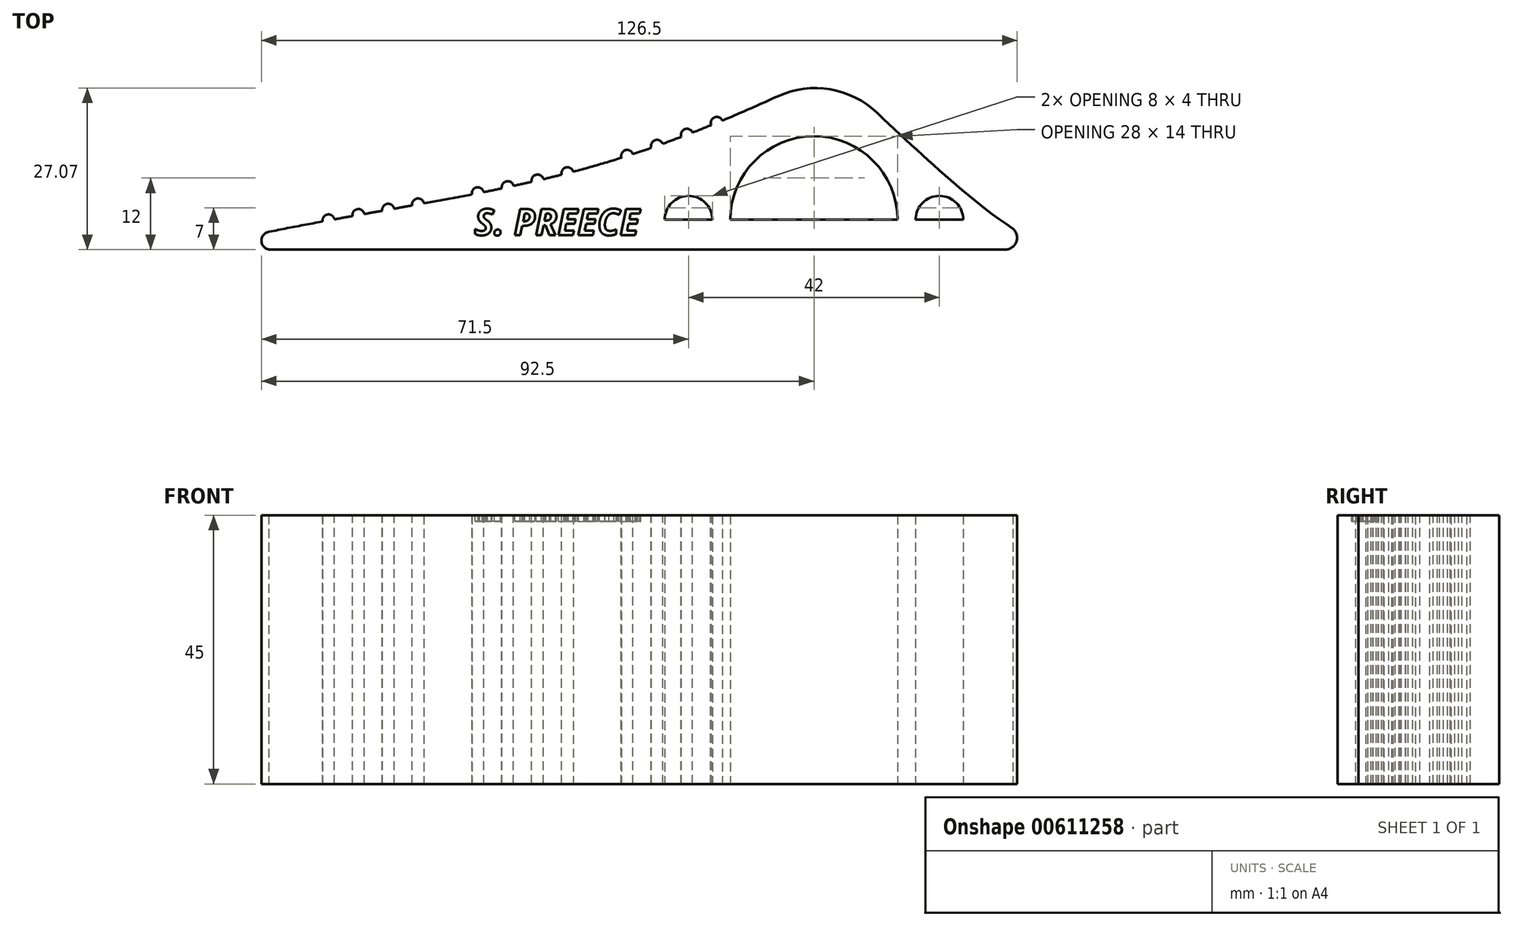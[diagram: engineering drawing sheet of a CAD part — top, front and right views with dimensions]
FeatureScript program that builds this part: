
annotation { "Feature Type Name" : "Feature", "Feature Type Description" : "" }
export const myFeature = defineFeature(function(context is Context, id is Id, definition is map)
    precondition{}
    {
        {
            var Q0;
            Q0=qCreatedBy(makeId("Top.planeOp"),FACE);
            var sketch = newSketch(context, id + "F0", { "sketchPlane" : qUnion([Q0])});
            skLineSegment(sketch, "E0", {"start": v(-38, 0) * mm, "end": v(85, 0) * mm});
            skPoint(sketch, "E1.visualSharp", {"position": v(-56.52, 0) * mm});
            skArc(sketch, "E1.filletArc", {"start": v(-38.27, 2.97) * mm, "mid": v(-39.5, 1.36) * mm, "end": v(-38, 0) * mm});
            skPoint(sketch, "E2.visualSharp", {"position": v(89.83, 0) * mm});
            skArc(sketch, "E2.filletArc", {"start": v(85, 0) * mm, "mid": v(86.88, 1.3) * mm, "end": v(86.3, 3.52) * mm});
            skLineSegment(sketch, "E3", {"start": v(39, 5) * mm, "end": v(67, 5) * mm});
            skArc(sketch, "E4", {"start": v(67, 5) * mm, "mid": v(53, 19) * mm, "end": v(39, 5) * mm});
            skLineSegment(sketch, "E5", {"start": v(28, 5) * mm, "end": v(36, 5) * mm});
            skArc(sketch, "E6", {"start": v(36, 5) * mm, "mid": v(32, 9) * mm, "end": v(28, 5) * mm});
            skArc(sketch, "E7.MirrorCS", {"start": v(70, 5) * mm, "mid": v(74, 9) * mm, "end": v(78, 5) * mm});
            skLineSegment(sketch, "E8.MirrorCS", {"start": v(78, 5) * mm, "end": v(70, 5) * mm});
            skFitSpline(sketch, "E9", {"points": [v(-38.27, 2.97) * mm, v(15.47, 13.8) * mm, v(56.42, 30.22) * mm], "startDerivative": vector(104, 21.18) * mm, "endDerivative": vector(77.97, 38.18) * mm});
            skPoint(sketch, "E10.1.internal.snap0", {"position": v(71.36, 16.87) * mm});
            skFitSpline(sketch, "E10", {"points": [v(56.42, 30.22) * mm, v(71.36, 15.67) * mm, v(86.3, 3.52) * mm], "startDerivative": vector(31.6, -34.36) * mm, "endDerivative": vector(35.04, -23.4) * mm});
            skArc(sketch, "E11.filletArc", {"start": v(63.6, 22.86) * mm, "mid": v(55.7, 26.85) * mm, "end": v(46.93, 25.7) * mm});
            skSolve(sketch);
        }
        {
            var Q0;
            Q0=makeQuery(id+"F0.imprint","IMPRINT",FACE,{"disambiguationData":[TD([[makeQuery(id+"F0.imprint","IMPRINT",EDGE,{"derivedFrom":sQuery(id+"F0.wireOp",EDGE,"E0")}),1.0]])]});
            extrude(context, id + "F1", {"entities" : qUnion([Q0]), "depth" : 45 * mm, "offsetDistance" : 25 * mm});
        }
        {
            var Q0;
            Q0=makeQuery(id+"F1.opExtrude","CAP_FACE",FACE,{"disambiguationData":[OSD([sQuery(id+"F0.wireOp",EDGE,"E0"),sQuery(id+"F0.wireOp",EDGE,"E1.filletArc"),sQuery(id+"F0.wireOp",EDGE,"E2.filletArc"),sQuery(id+"F0.wireOp",EDGE,"E3"),sQuery(id+"F0.wireOp",EDGE,"E4"),sQuery(id+"F0.wireOp",EDGE,"E5"),sQuery(id+"F0.wireOp",EDGE,"E6"),sQuery(id+"F0.wireOp",EDGE,"E7.MirrorCS"),sQuery(id+"F0.wireOp",EDGE,"E8.MirrorCS"),sQuery(id+"F0.wireOp",EDGE,"E9"),sQuery(id+"F0.wireOp",EDGE,"E10"),sQuery(id+"F0.wireOp",EDGE,"E11.filletArc")])],"isStart":false});
            var sketch = newSketch(context, id + "F2", { "sketchPlane" : qUnion([Q0])});
            skCircle(sketch, "E12", {"center": v(-28.27, 4.9) * mm, "radius": 1 * mm});
            skCircle(sketch, "E13", {"center": v(-23.27, 5.8) * mm, "radius": 1 * mm});
            skCircle(sketch, "E14", {"center": v(-18.27, 6.68) * mm, "radius": 1 * mm});
            skCircle(sketch, "E15", {"center": v(-13.27, 7.57) * mm, "radius": 1 * mm});
            skCircle(sketch, "E16", {"center": v(-3.27, 9.44) * mm, "radius": 1 * mm});
            skCircle(sketch, "E17", {"center": v(1.73, 10.46) * mm, "radius": 1 * mm});
            skCircle(sketch, "E18", {"center": v(6.73, 11.57) * mm, "radius": 1 * mm});
            skCircle(sketch, "E19", {"center": v(11.73, 12.8) * mm, "radius": 1 * mm});
            skCircle(sketch, "E20", {"center": v(21.73, 15.7) * mm, "radius": 1 * mm});
            skCircle(sketch, "E21", {"center": v(26.73, 17.4) * mm, "radius": 1 * mm});
            skCircle(sketch, "E22", {"center": v(31.73, 19.25) * mm, "radius": 1 * mm});
            skCircle(sketch, "E23", {"center": v(36.73, 21.24) * mm, "radius": 1 * mm});
            skSolve(sketch);
        }
        {
            var Q0;
            Q0 = qSketchRegion(id + "F2", true);
            var Q1;
            Q1=makeQuery(id+"F1.opExtrude","CAP_FACE",FACE,{"disambiguationData":[OSD([sQuery(id+"F0.wireOp",EDGE,"E0"),sQuery(id+"F0.wireOp",EDGE,"E1.filletArc"),sQuery(id+"F0.wireOp",EDGE,"E2.filletArc"),sQuery(id+"F0.wireOp",EDGE,"E3"),sQuery(id+"F0.wireOp",EDGE,"E4"),sQuery(id+"F0.wireOp",EDGE,"E5"),sQuery(id+"F0.wireOp",EDGE,"E6"),sQuery(id+"F0.wireOp",EDGE,"E7.MirrorCS"),sQuery(id+"F0.wireOp",EDGE,"E8.MirrorCS"),sQuery(id+"F0.wireOp",EDGE,"E9"),sQuery(id+"F0.wireOp",EDGE,"E10"),sQuery(id+"F0.wireOp",EDGE,"E11.filletArc")])],"isStart":true});
            extrude(context, id + "F3", {"entities" : qUnion([Q0]), "operationType" : NewBodyOperationType.ADD, "endBound" : BoundingType.UP_TO_SURFACE, "oppositeDirection" : true, "depth" : 25 * mm, "endBoundEntityFace" : qUnion([Q1]), "offsetDistance" : 25 * mm});
        }
        {
            var Q0;
            Q0=makeQuery(id+"F3.boolean.opBoolean","MERGE",FACE,{"derivedFrom":[makeQuery(id+"F1.opExtrude","CAP_FACE",FACE,{"disambiguationData":[OSD([sQuery(id+"F0.wireOp",EDGE,"E0"),sQuery(id+"F0.wireOp",EDGE,"E1.filletArc"),sQuery(id+"F0.wireOp",EDGE,"E2.filletArc"),sQuery(id+"F0.wireOp",EDGE,"E3"),sQuery(id+"F0.wireOp",EDGE,"E4"),sQuery(id+"F0.wireOp",EDGE,"E5"),sQuery(id+"F0.wireOp",EDGE,"E6"),sQuery(id+"F0.wireOp",EDGE,"E7.MirrorCS"),sQuery(id+"F0.wireOp",EDGE,"E8.MirrorCS"),sQuery(id+"F0.wireOp",EDGE,"E9"),sQuery(id+"F0.wireOp",EDGE,"E10"),sQuery(id+"F0.wireOp",EDGE,"E11.filletArc")])],"isStart":false}),makeQuery(id+"F3.opExtrude","CAP_FACE",FACE,{"disambiguationData":[OSD([sQuery(id+"F2.wireOp",EDGE,"E12")])],"isStart":true}),makeQuery(id+"F3.opExtrude","CAP_FACE",FACE,{"disambiguationData":[OSD([sQuery(id+"F2.wireOp",EDGE,"E13")])],"isStart":true}),makeQuery(id+"F3.opExtrude","CAP_FACE",FACE,{"disambiguationData":[OSD([sQuery(id+"F2.wireOp",EDGE,"E14")])],"isStart":true}),makeQuery(id+"F3.opExtrude","CAP_FACE",FACE,{"disambiguationData":[OSD([sQuery(id+"F2.wireOp",EDGE,"E15")])],"isStart":true}),makeQuery(id+"F3.opExtrude","CAP_FACE",FACE,{"disambiguationData":[OSD([sQuery(id+"F2.wireOp",EDGE,"E16")])],"isStart":true}),makeQuery(id+"F3.opExtrude","CAP_FACE",FACE,{"disambiguationData":[OSD([sQuery(id+"F2.wireOp",EDGE,"E17")])],"isStart":true}),makeQuery(id+"F3.opExtrude","CAP_FACE",FACE,{"disambiguationData":[OSD([sQuery(id+"F2.wireOp",EDGE,"E18")])],"isStart":true}),makeQuery(id+"F3.opExtrude","CAP_FACE",FACE,{"disambiguationData":[OSD([sQuery(id+"F2.wireOp",EDGE,"E19")])],"isStart":true}),makeQuery(id+"F3.opExtrude","CAP_FACE",FACE,{"disambiguationData":[OSD([sQuery(id+"F2.wireOp",EDGE,"E20")])],"isStart":true}),makeQuery(id+"F3.opExtrude","CAP_FACE",FACE,{"disambiguationData":[OSD([sQuery(id+"F2.wireOp",EDGE,"E21")])],"isStart":true}),makeQuery(id+"F3.opExtrude","CAP_FACE",FACE,{"disambiguationData":[OSD([sQuery(id+"F2.wireOp",EDGE,"E22")])],"isStart":true}),makeQuery(id+"F3.opExtrude","CAP_FACE",FACE,{"disambiguationData":[OSD([sQuery(id+"F2.wireOp",EDGE,"E23")])],"isStart":true})]});
            var sketch = newSketch(context, id + "F4", { "sketchPlane" : qUnion([Q0])});
            skText(sketch, "E24", { "text": "S. PREECE", "fontName": "OpenSans-BoldItalic.ttf"});
            const initialGuessF4  = {"E24": [-0.00385, 0.00242, 1, 0, 0.00442]};
            skSetInitialGuess(sketch, initialGuessF4);
            skSolve(sketch);
        }
        {
            var Q0;
            Q0 = qSketchRegion(id + "F4", true);
            extrude(context, id + "F5", {"entities" : qUnion([Q0]), "operationType" : NewBodyOperationType.REMOVE, "oppositeDirection" : true, "depth" : 1 * mm, "offsetDistance" : 25 * mm});
        }
    });
